# Revit family: ITK Проходной адаптер LC-LC_SM-MM_APC_Dupplex
name_source: partatom
category: Обобщенные модели
units: mm (PartAtom-declared; Revit-internal decimal feet)

## family parameters
Всегда вертикально = Да
Может служить основой для арматурных стержней = Нет
На основе рабочей плоскости = Нет
Общий = Нет
При загрузке вырезать с полостями = Нет
Размер круглого соединителя = Использовать диаметр
Тип детали = Нормальный
Точка расчета площади = Нет

## types (2) — shared parameters
ADSK_URL страницы изделия = https://www.itk-group.ru
ADSK_Версия Revit = 2019
ADSK_Версия семейства = 1.0
ADSK_Группирование = I. ЩИТЫ И ПУЛЬТЫ
ADSK_Единица измерения = шт
ADSK_Завод-изготовитель = IEK
ADSK_Материал наименование = Пластик
IEK_URL = https://www.itk-group.ru
IEK_Описание = Качественное, надежное соединение для передачи сигнала.
Большой ресурс включений - 500.
Высококачественный материал продукции.
Большой диапазон температур от -40°C до +75°C.
KSI_CMa_Строительные материалы = 01.7.14.02
KSI_CPr_Строительные изделия = 61.1.03.04
URL = https://www.iek.ru
Изготовитель = ITK
Ширина = 35 мм
zero-valued in all types: ADSK_Масса

## per-type parameters (varying)
| type | ADSK_Код изделия | ADSK_Наименование | IEK_Цена за единицу | Материал |
| APC | FC1-LCALCA2C-SM | ITK Проходной адаптер LC-LC, (SM/MM), APC, (Duplex) | 92.08 | Пластик синий |
| UPC | FC1-LCULCU2C-SM | ITK Проходной адаптер LC-LC, (SM/MM), UPC, (Duplex) | 90.34 | Пластик зеленый |
